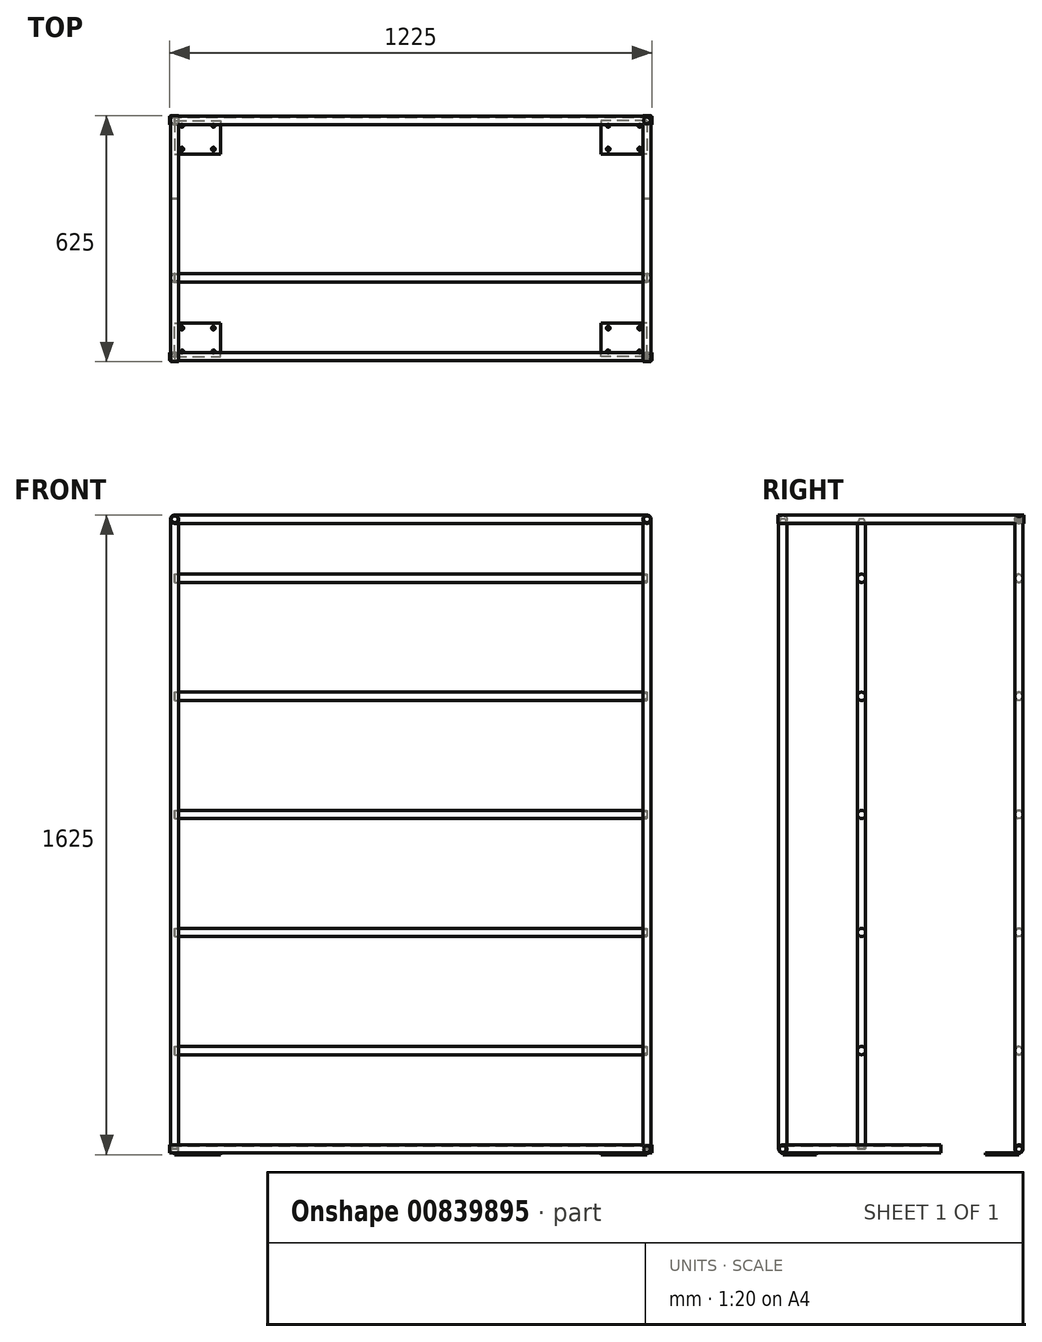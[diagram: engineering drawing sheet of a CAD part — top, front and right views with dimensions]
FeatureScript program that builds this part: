
annotation { "Feature Type Name" : "Feature", "Feature Type Description" : "" }
export const myFeature = defineFeature(function(context is Context, id is Id, definition is map)
    precondition{}
    {
        {
            var Q0;
            Q0=qCreatedBy(makeId("Top.planeOp"),FACE);
            var sketch = newSketch(context, id + "F0", { "sketchPlane" : qUnion([Q0])});
            skLineSegment(sketch, "E0.bottom", {"start": v(-576.39, 329) * mm, "end": v(602.61, 329) * mm});
            skLineSegment(sketch, "E0.top", {"start": v(-576.39, -271) * mm, "end": v(602.61, -271) * mm});
            skLineSegment(sketch, "E0.left", {"start": v(-586.89, 318.5) * mm, "end": v(-586.89, -60.5) * mm});
            skLineSegment(sketch, "E0.right", {"start": v(613.11, 318.5) * mm, "end": v(613.11, -60.5) * mm});
            skCircle(sketch, "E1", {"center": v(-586.89, 329) * mm, "radius": 10.5 * mm});
            skCircle(sketch, "E2", {"center": v(613.11, 329) * mm, "radius": 10.5 * mm});
            skCircle(sketch, "E3", {"center": v(613.11, -271) * mm, "radius": 10.5 * mm});
            skCircle(sketch, "E4", {"center": v(-586.89, -271) * mm, "radius": 10.5 * mm});
            skCircle(sketch, "E5", {"center": v(613.11, -71) * mm, "radius": 10.5 * mm});
            skCircle(sketch, "E6", {"center": v(-586.89, -71) * mm, "radius": 10.5 * mm});
            skLineSegment(sketch, "E7.trimOffspring", {"start": v(-586.89, -81.5) * mm, "end": v(-586.89, -260.5) * mm});
            skLineSegment(sketch, "E8.trimOffspring", {"start": v(613.11, -81.5) * mm, "end": v(613.11, -260.5) * mm});
            skSolve(sketch);
        }
        {
            var Q0;
            {var subQ0=sQuery(id+"F0.wireOp",EDGE,"E1");var subQ1=makeQuery(id+"F0.imprint","INTERSECT",VERTEX,{"derivedFrom":[sQuery(id+"F0.wireOp",EDGE,"E0.bottom"),subQ0]});Q0=makeQuery(id+"F0.imprint","IMPRINT",FACE,{"disambiguationData":[TD([[makeQuery(id+"F0.imprint","IMPRINT",EDGE,{"disambiguationData":[TD([[subQ1,-1.0]])],"derivedFrom":subQ0}),1.0]])]});}
            var Q1;
            {var subQ0=sQuery(id+"F0.wireOp",EDGE,"E2");var subQ1=makeQuery(id+"F0.imprint","INTERSECT",VERTEX,{"derivedFrom":[sQuery(id+"F0.wireOp",EDGE,"E0.bottom"),subQ0]});Q1=makeQuery(id+"F0.imprint","IMPRINT",FACE,{"disambiguationData":[TD([[makeQuery(id+"F0.imprint","IMPRINT",EDGE,{"disambiguationData":[TD([[subQ1,-1.0]])],"derivedFrom":subQ0}),1.0]])]});}
            var Q2;
            {var subQ0=sQuery(id+"F0.wireOp",EDGE,"E3");var subQ1=makeQuery(id+"F0.imprint","INTERSECT",VERTEX,{"derivedFrom":[sQuery(id+"F0.wireOp",EDGE,"E0.top"),subQ0]});Q2=makeQuery(id+"F0.imprint","IMPRINT",FACE,{"disambiguationData":[TD([[makeQuery(id+"F0.imprint","IMPRINT",EDGE,{"disambiguationData":[TD([[subQ1,1.0]])],"derivedFrom":subQ0}),1.0]])]});}
            var Q3;
            {var subQ0=sQuery(id+"F0.wireOp",EDGE,"E4");var subQ1=makeQuery(id+"F0.imprint","INTERSECT",VERTEX,{"derivedFrom":[sQuery(id+"F0.wireOp",EDGE,"E0.top"),subQ0]});Q3=makeQuery(id+"F0.imprint","IMPRINT",FACE,{"disambiguationData":[TD([[makeQuery(id+"F0.imprint","IMPRINT",EDGE,{"disambiguationData":[TD([[subQ1,-1.0]])],"derivedFrom":subQ0}),1.0]])]});}
            var Q4;
            {var subQ0=sQuery(id+"F0.wireOp",EDGE,"E5");var subQ1=makeQuery(id+"F0.imprint","INTERSECT",VERTEX,{"derivedFrom":[sQuery(id+"F0.wireOp",EDGE,"E0.right"),subQ0]});Q4=makeQuery(id+"F0.imprint","IMPRINT",FACE,{"disambiguationData":[TD([[makeQuery(id+"F0.imprint","IMPRINT",EDGE,{"disambiguationData":[TD([[subQ1,-1.0]])],"derivedFrom":subQ0}),1.0]])]});}
            var Q5;
            {var subQ0=sQuery(id+"F0.wireOp",EDGE,"E6");var subQ1=makeQuery(id+"F0.imprint","INTERSECT",VERTEX,{"derivedFrom":[sQuery(id+"F0.wireOp",EDGE,"E0.left"),subQ0]});Q5=makeQuery(id+"F0.imprint","IMPRINT",FACE,{"disambiguationData":[TD([[makeQuery(id+"F0.imprint","IMPRINT",EDGE,{"disambiguationData":[TD([[subQ1,-1.0]])],"derivedFrom":subQ0}),1.0]])]});}
            extrude(context, id + "F1", {"entities" : qUnion([Q0, Q1, Q2, Q3, Q4, Q5]), "depth" : 1600 * mm, "offsetDistance" : 25 * mm});
        }
        {
            var Q0;
            Q0=sQuery(id+"F0.wireOp",EDGE,"E0.bottom");
            cPlane(context, id + "F2", {"entities" : qUnion([Q0]), "cplaneType" : CPlaneType.MID_PLANE, "offset" : 25 * mm, "width" : 150 * mm, "height" : 150 * mm});
        }
        {
            var Q0;
            Q0=qCreatedBy(id+"F2.planeOp",FACE);
            var sketch = newSketch(context, id + "F3", { "sketchPlane" : qUnion([Q0])});
            skCircle(sketch, "E9", {"center": v(329, 0) * mm, "radius": 10.5 * mm});
            skCircle(sketch, "E10", {"center": v(-271, 0) * mm, "radius": 10.5 * mm});
            skSolve(sketch);
        }
        {
            var Q0;
            Q0 = qSketchRegion(id + "F3", true);
            extrude(context, id + "F4", {"entities" : qUnion([Q0]), "depth" : 612.5 * mm, "offsetDistance" : 25 * mm, "hasSecondDirection" : true, "secondDirectionOppositeDirection" : true, "secondDirectionDepth" : 612.5 * mm});
        }
        {
            var Q0;
            Q0=sQuery(id+"F0.wireOp",EDGE,"E0.right");
            cPlane(context, id + "F5", {"entities" : qUnion([Q0]), "cplaneType" : CPlaneType.MID_PLANE, "offset" : 25 * mm, "width" : 150 * mm, "height" : 150 * mm});
        }
        {
            var Q0;
            Q0=qCreatedBy(id+"F5.planeOp",FACE);
            var sketch = newSketch(context, id + "F6", { "sketchPlane" : qUnion([Q0])});
            skCircle(sketch, "E11", {"center": v(613.11, 0) * mm, "radius": 10.5 * mm});
            skCircle(sketch, "E12", {"center": v(-586.89, 0) * mm, "radius": 10.5 * mm});
            skSolve(sketch);
        }
        {
            var Q0;
            Q0 = qSketchRegion(id + "F6", true);
            extrude(context, id + "F7", {"entities" : qUnion([Q0]), "oppositeDirection" : true, "depth" : 38.75 / 20 * mm, "offsetDistance" : 25 * mm, "hasSecondDirection" : true, "secondDirectionOppositeDirection" : false, "secondDirectionDepth" : 400 * mm});
        }
        {
            var Q0;
            Q0=makeQuery(id+"F1.opExtrude","SWEPT_FACE",FACE,{"disambiguationData":[OSD([sQuery(id+"F0.wireOp",EDGE,"E2")])]});
            var Q1;
            Q1=makeQuery(id+"F1.opExtrude","SWEPT_FACE",FACE,{"disambiguationData":[OSD([sQuery(id+"F0.wireOp",EDGE,"E1")])]});
            cPlane(context, id + "F8", {"entities" : qUnion([Q0, Q1]), "cplaneType" : CPlaneType.LINE_ANGLE, "offset" : 25 * mm, "angle" : 0 * degree, "width" : 150 * mm, "height" : 150 * mm});
        }
        {
            var Q0;
            Q0=qCreatedBy(id+"F8.planeOp",FACE);
            var sketch = newSketch(context, id + "F9", { "sketchPlane" : qUnion([Q0])});
            skLineSegment(sketch, "E13", {"start": v(-613.11, 0) * mm, "end": v(-613.11, 1600) * mm});
            skLineSegment(sketch, "E14", {"start": v(586.89, 0) * mm, "end": v(586.89, 1600) * mm});
            skLineSegment(sketch, "E15", {"start": v(-613.11, 250) * mm, "end": v(586.89, 250) * mm});
            skLineSegment(sketch, "E16", {"start": v(-613.11, 550) * mm, "end": v(586.89, 550) * mm});
            skLineSegment(sketch, "E17", {"start": v(-613.11, 850) * mm, "end": v(586.89, 850) * mm});
            skLineSegment(sketch, "E18", {"start": v(-613.11, 1150) * mm, "end": v(586.89, 1150) * mm});
            skLineSegment(sketch, "E19", {"start": v(-613.11, 1450) * mm, "end": v(586.89, 1450) * mm});
            skLineSegment(sketch, "E20", {"start": v(-613.11, 1600) * mm, "end": v(586.89, 1600) * mm});
            skSolve(sketch);
        }
        {
            var Q0;
            Q0=qCreatedBy(id+"F8.planeOp",FACE);
            cPlane(context, id + "F10", {"entities" : qUnion([Q0]), "cplaneType" : CPlaneType.OFFSET, "offset" : 400 * mm, "oppositeDirection" : true, "width" : 150 * mm, "height" : 150 * mm});
        }
        {
            var Q0;
            Q0=qCreatedBy(id+"F10.planeOp",FACE);
            var sketch = newSketch(context, id + "F11", { "sketchPlane" : qUnion([Q0])});
            skLineSegment(sketch, "E21", {"start": v(-613.11, 0) * mm, "end": v(-613.11, 1600) * mm});
            skLineSegment(sketch, "E22", {"start": v(586.89, 0) * mm, "end": v(586.89, 1600) * mm});
            skLineSegment(sketch, "E23", {"start": v(-613.11, 250) * mm, "end": v(586.89, 250) * mm});
            skLineSegment(sketch, "E24", {"start": v(-613.11, 550) * mm, "end": v(586.89, 550) * mm});
            skLineSegment(sketch, "E25", {"start": v(-613.11, 850) * mm, "end": v(586.89, 850) * mm});
            skLineSegment(sketch, "E26", {"start": v(-613.11, 1150) * mm, "end": v(586.89, 1150) * mm});
            skLineSegment(sketch, "E27", {"start": v(-613.11, 1450) * mm, "end": v(586.89, 1450) * mm});
            skSolve(sketch);
        }
        {
            var Q0;
            Q0=qCreatedBy(id+"F8.planeOp",FACE);
            cPlane(context, id + "F12", {"entities" : qUnion([Q0]), "cplaneType" : CPlaneType.OFFSET, "offset" : 600 * mm, "oppositeDirection" : true, "width" : 150 * mm, "height" : 150 * mm});
        }
        {
            var Q0;
            Q0=qCreatedBy(id+"F12.planeOp",FACE);
            var sketch = newSketch(context, id + "F13", { "sketchPlane" : qUnion([Q0])});
            skLineSegment(sketch, "E28", {"start": v(-613.11, 0) * mm, "end": v(-613.11, 1600) * mm});
            skLineSegment(sketch, "E29", {"start": v(586.89, 0) * mm, "end": v(586.89, 1600) * mm});
            skLineSegment(sketch, "E30", {"start": v(-613.11, 1600) * mm, "end": v(586.89, 1600) * mm});
            skSolve(sketch);
        }
        {
            var Q0;
            Q0=sQuery(id+"F13.wireOp",EDGE,"E30");
            cPlane(context, id + "F14", {"entities" : qUnion([Q0]), "cplaneType" : CPlaneType.MID_PLANE, "offset" : 25 * mm, "width" : 150 * mm, "height" : 150 * mm});
        }
        {
            var Q0;
            Q0=qCreatedBy(id+"F14.planeOp",FACE);
            var sketch = newSketch(context, id + "F15", { "sketchPlane" : qUnion([Q0])});
            skCircle(sketch, "E31", {"center": v(271, 1600) * mm, "radius": 10.5 * mm});
            skCircle(sketch, "E32", {"center": v(71, 1450) * mm, "radius": 10.5 * mm});
            skCircle(sketch, "E33", {"center": v(71, 1150) * mm, "radius": 10.5 * mm});
            skCircle(sketch, "E34", {"center": v(71, 850) * mm, "radius": 10.5 * mm});
            skCircle(sketch, "E35", {"center": v(71, 550) * mm, "radius": 10.5 * mm});
            skCircle(sketch, "E36", {"center": v(71, 250) * mm, "radius": 10.5 * mm});
            skCircle(sketch, "E37", {"center": v(-329, 1600) * mm, "radius": 10.5 * mm});
            skCircle(sketch, "E38", {"center": v(-329, 1450) * mm, "radius": 10.5 * mm});
            skCircle(sketch, "E39", {"center": v(-329, 1150) * mm, "radius": 10.5 * mm});
            skCircle(sketch, "E40", {"center": v(-329, 850) * mm, "radius": 10.5 * mm});
            skCircle(sketch, "E41", {"center": v(-329, 550) * mm, "radius": 10.5 * mm});
            skCircle(sketch, "E42", {"center": v(-329, 250) * mm, "radius": 10.5 * mm});
            skSolve(sketch);
        }
        {
            var Q0;
            Q0 = qSketchRegion(id + "F15", true);
            extrude(context, id + "F16", {"entities" : qUnion([Q0]), "depth" : 600 * mm, "offsetDistance" : 25 * mm, "hasSecondDirection" : true, "secondDirectionOppositeDirection" : true, "secondDirectionDepth" : 600 * mm});
        }
        {
            var Q0;
            Q0=makeQuery(id+"F1.opExtrude","SWEPT_FACE",FACE,{"disambiguationData":[OSD([sQuery(id+"F0.wireOp",EDGE,"E1")])]});
            var Q1;
            Q1=makeQuery(id+"F16.opExtrude","SWEPT_FACE",FACE,{"disambiguationData":[OSD([sQuery(id+"F15.wireOp",EDGE,"E37")])]});
            cPlane(context, id + "F17", {"entities" : qUnion([Q0, Q1]), "cplaneType" : CPlaneType.LINE_ANGLE, "offset" : 25 * mm, "angle" : 0 * degree, "width" : 150 * mm, "height" : 150 * mm});
        }
        {
            var Q0;
            Q0=qCreatedBy(id+"F17.planeOp",FACE);
            var sketch = newSketch(context, id + "F18", { "sketchPlane" : qUnion([Q0])});
            skCircle(sketch, "E43", {"center": v(-586.89, 1600) * mm, "radius": 10.5 * mm});
            skCircle(sketch, "E44", {"center": v(613.11, 1600) * mm, "radius": 10.5 * mm});
            skSolve(sketch);
        }
        {
            var Q0;
            Q0 = qSketchRegion(id + "F18", true);
            extrude(context, id + "F19", {"entities" : qUnion([Q0]), "oppositeDirection" : true, "depth" : 12.5 * mm, "offsetDistance" : 25 * mm, "hasSecondDirection" : true, "secondDirectionOppositeDirection" : false, "secondDirectionDepth" : 612.5 * mm});
        }
        {
            var Q0;
            Q0=qCreatedBy(makeId("Top.planeOp"),FACE);
            cPlane(context, id + "F20", {"entities" : qUnion([Q0]), "cplaneType" : CPlaneType.OFFSET, "offset" : 10.5 * mm, "oppositeDirection" : true, "width" : 150 * mm, "height" : 150 * mm});
        }
        {
            var Q0;
            Q0=qCreatedBy(id+"F20.planeOp",FACE);
            var sketch = newSketch(context, id + "F21", { "sketchPlane" : qUnion([Q0])});
            skLineSegment(sketch, "E45.bottom", {"start": v(-586.89, -271) * mm, "end": v(-469.89, -271) * mm});
            skLineSegment(sketch, "E45.top", {"start": v(-586.89, -186) * mm, "end": v(-469.89, -186) * mm});
            skLineSegment(sketch, "E45.left", {"start": v(-586.89, -271) * mm, "end": v(-586.89, -186) * mm});
            skLineSegment(sketch, "E45.right", {"start": v(-469.89, -271) * mm, "end": v(-469.89, -186) * mm});
            skLineSegment(sketch, "E46.bottom", {"start": v(-568.39, -258.5) * mm, "end": v(-488.39, -258.5) * mm, "construction": true});
            skLineSegment(sketch, "E46.top", {"start": v(-568.39, -198.5) * mm, "end": v(-488.39, -198.5) * mm, "construction": true});
            skLineSegment(sketch, "E46.left", {"start": v(-568.39, -258.5) * mm, "end": v(-568.39, -198.5) * mm, "construction": true});
            skLineSegment(sketch, "E46.right", {"start": v(-488.39, -258.5) * mm, "end": v(-488.39, -198.5) * mm, "construction": true});
            skCircle(sketch, "E47", {"center": v(-568.39, -258.5) * mm, "radius": 4.5 * mm});
            skCircle(sketch, "E48", {"center": v(-488.39, -258.5) * mm, "radius": 4.5 * mm});
            skCircle(sketch, "E49", {"center": v(-488.39, -198.5) * mm, "radius": 4.5 * mm});
            skCircle(sketch, "E50", {"center": v(-568.39, -198.5) * mm, "radius": 4.5 * mm});
            skLineSegment(sketch, "E51", {"start": v(-528.39, -258.5) * mm, "end": v(-528.39, -198.5) * mm, "construction": true});
            skLineSegment(sketch, "E52", {"start": v(-568.39, -228.5) * mm, "end": v(-488.39, -228.5) * mm, "construction": true});
            skLineSegment(sketch, "E53", {"start": v(-528.39, -271) * mm, "end": v(-528.39, -186) * mm, "construction": true});
            skLineSegment(sketch, "E54", {"start": v(-586.89, -228.5) * mm, "end": v(-469.89, -228.5) * mm, "construction": true});
            skLineSegment(sketch, "E55", {"start": v(13.11, -271) * mm, "end": v(13.11, 329) * mm, "construction": true});
            skLineSegment(sketch, "E56", {"start": v(13.11, 29) * mm, "end": v(-210.36, 29) * mm, "construction": true});
            skLineSegment(sketch, "E57.MirrorCS", {"start": v(613.11, -186) * mm, "end": v(496.11, -186) * mm});
            skLineSegment(sketch, "E58.MirrorCS", {"start": v(496.11, -271) * mm, "end": v(496.11, -186) * mm});
            skLineSegment(sketch, "E59.MirrorCS", {"start": v(613.11, -271) * mm, "end": v(496.11, -271) * mm});
            skLineSegment(sketch, "E60.MirrorCS", {"start": v(613.11, -271) * mm, "end": v(613.11, -186) * mm});
            skCircle(sketch, "E61.MirrorC", {"center": v(594.61, -258.5) * mm, "radius": 4.5 * mm});
            skCircle(sketch, "E62.MirrorC", {"center": v(514.61, -258.5) * mm, "radius": 4.5 * mm});
            skCircle(sketch, "E63.MirrorC", {"center": v(514.61, -198.5) * mm, "radius": 4.5 * mm});
            skCircle(sketch, "E64.MirrorC", {"center": v(594.61, -198.5) * mm, "radius": 4.5 * mm});
            skLineSegment(sketch, "E65.MirrorCS", {"start": v(-586.89, 244) * mm, "end": v(-469.89, 244) * mm});
            skLineSegment(sketch, "E66.MirrorCS", {"start": v(-469.89, 329) * mm, "end": v(-469.89, 244) * mm});
            skLineSegment(sketch, "E67.MirrorCS", {"start": v(-586.89, 329) * mm, "end": v(-469.89, 329) * mm});
            skLineSegment(sketch, "E68.MirrorCS", {"start": v(-586.89, 329) * mm, "end": v(-586.89, 244) * mm});
            skCircle(sketch, "E69.MirrorC", {"center": v(-568.39, 316.5) * mm, "radius": 4.5 * mm});
            skCircle(sketch, "E70.MirrorC", {"center": v(-488.39, 316.5) * mm, "radius": 4.5 * mm});
            skCircle(sketch, "E71.MirrorC", {"center": v(-488.39, 256.5) * mm, "radius": 4.5 * mm});
            skCircle(sketch, "E72.MirrorC", {"center": v(-568.39, 256.5) * mm, "radius": 4.5 * mm});
            skCircle(sketch, "E73.MirrorC", {"center": v(514.61, 316.5) * mm, "radius": 4.5 * mm});
            skCircle(sketch, "E74.MirrorC", {"center": v(594.61, 316.5) * mm, "radius": 4.5 * mm});
            skCircle(sketch, "E75.MirrorC", {"center": v(594.61, 256.5) * mm, "radius": 4.5 * mm});
            skCircle(sketch, "E76.MirrorC", {"center": v(514.61, 256.5) * mm, "radius": 4.5 * mm});
            skLineSegment(sketch, "E77.MirrorCS", {"start": v(613.11, 244) * mm, "end": v(496.11, 244) * mm});
            skLineSegment(sketch, "E78.MirrorCS", {"start": v(496.11, 329) * mm, "end": v(496.11, 244) * mm});
            skLineSegment(sketch, "E79.MirrorCS", {"start": v(613.11, 329) * mm, "end": v(496.11, 329) * mm});
            skLineSegment(sketch, "E80.MirrorCS", {"start": v(613.11, 329) * mm, "end": v(613.11, 244) * mm});
            skSolve(sketch);
        }
        {
            var Q0;
            Q0 = qSketchRegion(id + "F21", true);
            extrude(context, id + "F22", {"entities" : qUnion([Q0]), "oppositeDirection" : true, "depth" : 4 * mm, "offsetDistance" : 25 * mm});
        }
        {
            var Q0;
            Q0=makeQuery(id+"F19.opExtrude","CAP_FACE",FACE,{"disambiguationData":[OSD([sQuery(id+"F18.wireOp",EDGE,"E44")])],"isStart":true});
            var sketch = newSketch(context, id + "F23", { "sketchPlane" : qUnion([Q0])});
            skCircle(sketch, "E81", {"center": v(613.11, 1600) * mm, "radius": 8.5 * mm});
            skSolve(sketch);
        }
        {
            var Q0;
            Q0=makeQuery(id+"F23.imprint","IMPRINT",FACE,{"disambiguationData":[TD([[makeQuery(id+"F23.imprint","IMPRINT",EDGE,{"derivedFrom":sQuery(id+"F23.wireOp",EDGE,"E81")}),1.0]])]});
            extrude(context, id + "F24", {"entities" : qUnion([Q0]), "operationType" : NewBodyOperationType.REMOVE, "oppositeDirection" : true, "depth" : 700 * mm, "offsetDistance" : 25 * mm});
        }
        {
            var Q0;
            Q0=makeQuery(id+"F19.opExtrude","CAP_FACE",FACE,{"disambiguationData":[OSD([sQuery(id+"F18.wireOp",EDGE,"E43")])],"isStart":true});
            var sketch = newSketch(context, id + "F25", { "sketchPlane" : qUnion([Q0])});
            skCircle(sketch, "E82", {"center": v(-586.89, 1600) * mm, "radius": 8.5 * mm});
            skSolve(sketch);
        }
        {
            var Q0;
            Q0 = qSketchRegion(id + "F25", true);
            extrude(context, id + "F26", {"entities" : qUnion([Q0]), "operationType" : NewBodyOperationType.REMOVE, "oppositeDirection" : true, "depth" : 700 * mm, "offsetDistance" : 25 * mm});
        }
        {
            var Q0;
            Q0=makeQuery(id+"F4.opExtrude","CAP_FACE",FACE,{"disambiguationData":[OSD([sQuery(id+"F3.wireOp",EDGE,"E10")])],"isStart":false});
            var sketch = newSketch(context, id + "F27", { "sketchPlane" : qUnion([Q0])});
            skCircle(sketch, "E83", {"center": v(-271, 0) * mm, "radius": 8.5 * mm});
            skSolve(sketch);
        }
        {
            var Q0;
            Q0 = qSketchRegion(id + "F27", true);
            extrude(context, id + "F28", {"entities" : qUnion([Q0]), "operationType" : NewBodyOperationType.REMOVE, "oppositeDirection" : true, "depth" : 1300 * mm, "offsetDistance" : 25 * mm});
        }
        {
            var Q0;
            Q0=makeQuery(id+"F4.opExtrude","CAP_FACE",FACE,{"disambiguationData":[OSD([sQuery(id+"F3.wireOp",EDGE,"E9")])],"isStart":false});
            var sketch = newSketch(context, id + "F29", { "sketchPlane" : qUnion([Q0])});
            skCircle(sketch, "E84", {"center": v(329, 0) * mm, "radius": 8.5 * mm});
            skSolve(sketch);
        }
        {
            var Q0;
            Q0 = qSketchRegion(id + "F29", true);
            extrude(context, id + "F30", {"entities" : qUnion([Q0]), "operationType" : NewBodyOperationType.REMOVE, "oppositeDirection" : true, "depth" : 1600 * mm, "offsetDistance" : 25 * mm});
        }
        {
            var Q0;
            Q0=makeQuery(id+"F7.opExtrude","CAP_FACE",FACE,{"disambiguationData":[OSD([sQuery(id+"F6.wireOp",EDGE,"E11")])],"isStart":false});
            var sketch = newSketch(context, id + "F31", { "sketchPlane" : qUnion([Q0])});
            skCircle(sketch, "E85", {"center": v(-613.11, 0) * mm, "radius": 8.5 * mm});
            skSolve(sketch);
        }
        {
            var Q0;
            Q0 = qSketchRegion(id + "F31", true);
            extrude(context, id + "F32", {"entities" : qUnion([Q0]), "operationType" : NewBodyOperationType.REMOVE, "oppositeDirection" : true, "depth" : 1600 * mm, "offsetDistance" : 25 * mm});
        }
        {
            var Q0;
            Q0=makeQuery(id+"F1.opExtrude","CAP_FACE",FACE,{"disambiguationData":[OSD([sQuery(id+"F0.wireOp",EDGE,"E2")])],"isStart":true});
            var sketch = newSketch(context, id + "F33", { "sketchPlane" : qUnion([Q0])});
            skCircle(sketch, "E86", {"center": v(613.11, -329) * mm, "radius": 8.5 * mm});
            skSolve(sketch);
        }
        {
            var Q0;
            Q0 = qSketchRegion(id + "F33", true);
            extrude(context, id + "F34", {"entities" : qUnion([Q0]), "operationType" : NewBodyOperationType.REMOVE, "oppositeDirection" : true, "depth" : 1700 * mm, "offsetDistance" : 25 * mm});
        }
    });
